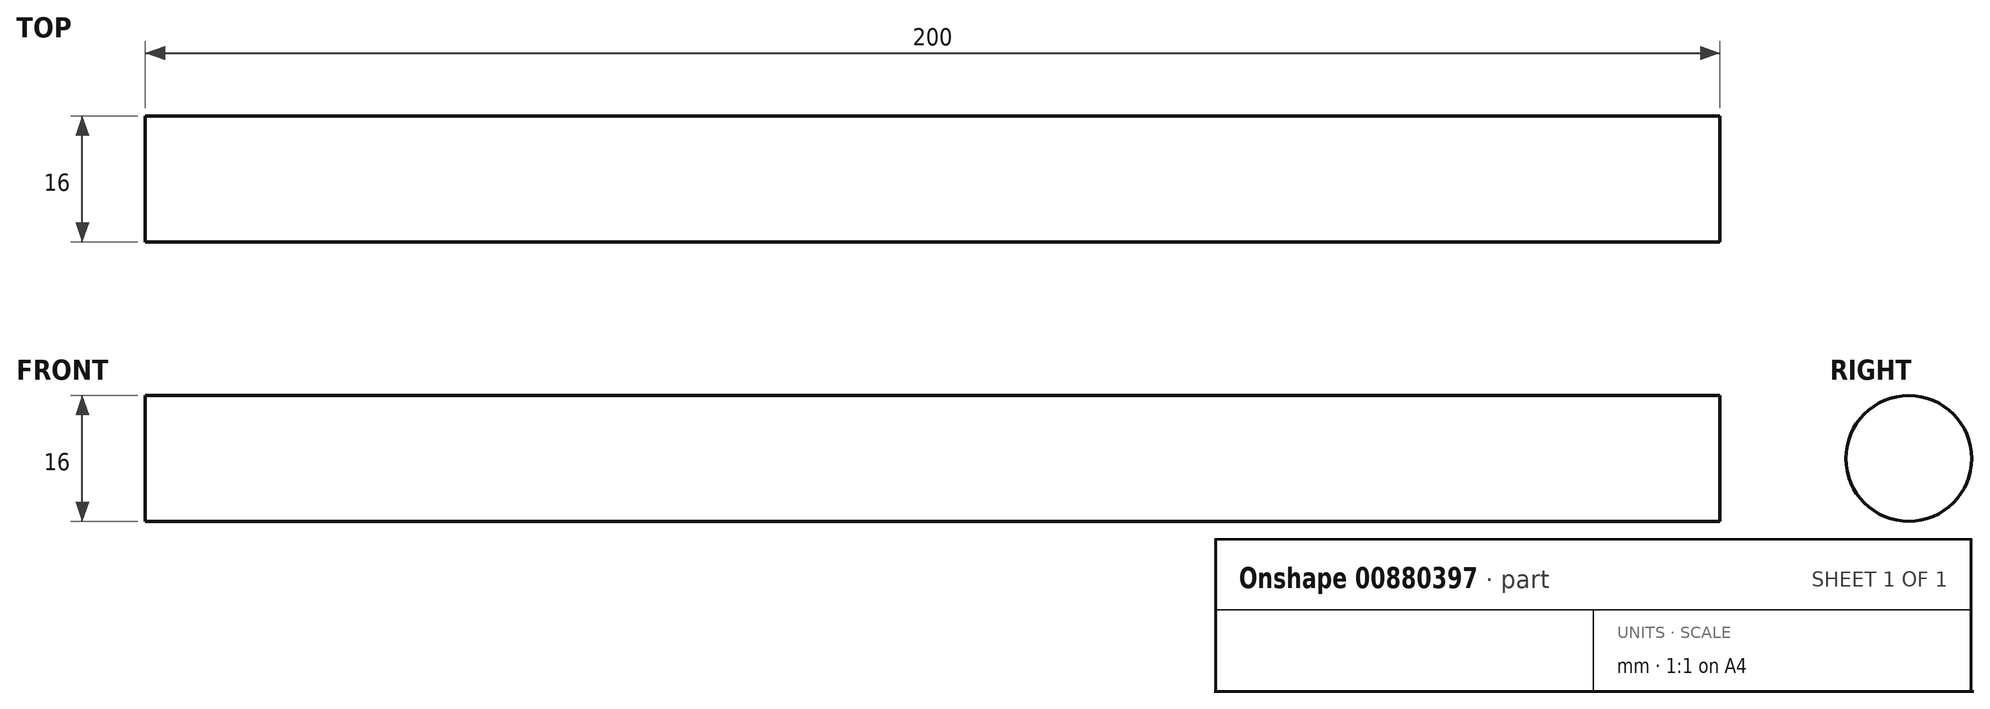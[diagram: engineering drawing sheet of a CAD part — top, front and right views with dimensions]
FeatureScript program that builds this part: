
annotation { "Feature Type Name" : "Feature", "Feature Type Description" : "" }
export const myFeature = defineFeature(function(context is Context, id is Id, definition is map)
    precondition{}
    {
        {
            var Q0;
            Q0=qCreatedBy(makeId("Right.planeOp"),FACE);
            var sketch = newSketch(context, id + "F0", { "sketchPlane" : qUnion([Q0])});
            skCircle(sketch, "E0", {"center": v(0, 0) * mm, "radius": 8 * mm});
            skSolve(sketch);
        }
        {
            var Q0;
            Q0 = qSketchRegion(id + "F0", true);
            extrude(context, id + "F1", {"entities" : qUnion([Q0]), "depth" : 200 * mm, "offsetDistance" : 25 * mm});
        }
    });
